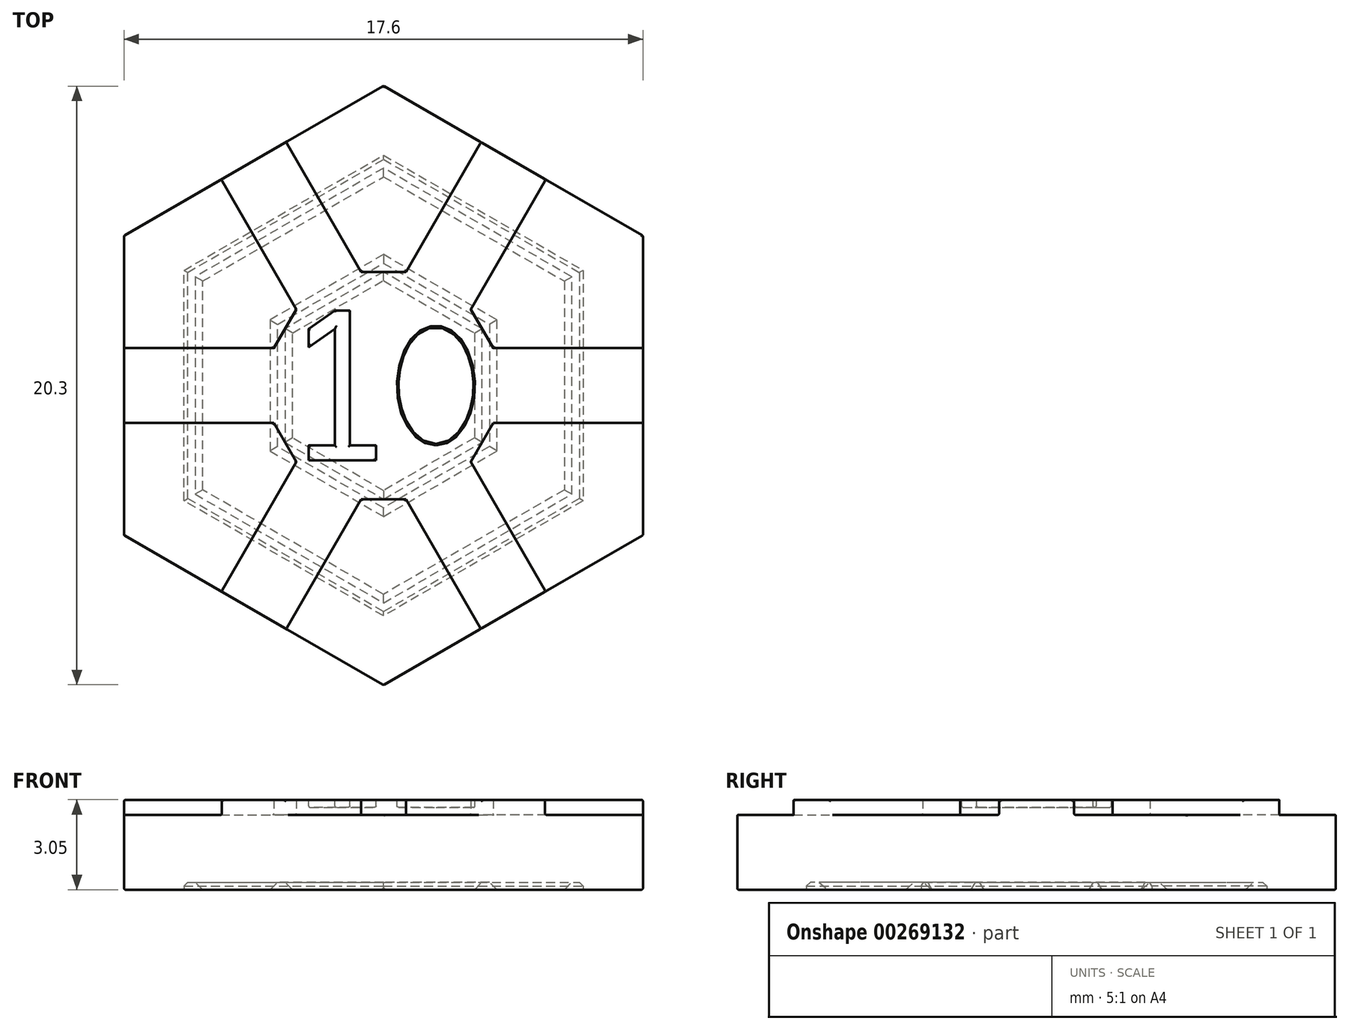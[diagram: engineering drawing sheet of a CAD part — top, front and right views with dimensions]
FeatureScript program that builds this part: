
annotation { "Feature Type Name" : "Feature", "Feature Type Description" : "" }
export const myFeature = defineFeature(function(context is Context, id is Id, definition is map)
    precondition{}
    {
        {
            var Q0;
            Q0=qCreatedBy(makeId("Top.planeOp"),FACE);
            var sketch = newSketch(context, id + "F0", { "sketchPlane" : qUnion([Q0])});
            skLineSegment(sketch, "E0", {"start": v(-8.8, -5.08) * mm, "end": v(-8.8, 5.08) * mm});
            skLineSegment(sketch, "E1", {"start": v(-8.8, 5.08) * mm, "end": v(0, 10.16) * mm});
            skLineSegment(sketch, "E2", {"start": v(0, 10.16) * mm, "end": v(8.8, 5.08) * mm});
            skLineSegment(sketch, "E3", {"start": v(8.8, 5.08) * mm, "end": v(8.8, -5.08) * mm});
            skLineSegment(sketch, "E4", {"start": v(8.8, -5.08) * mm, "end": v(0, -10.16) * mm});
            skLineSegment(sketch, "E5", {"start": v(0, -10.16) * mm, "end": v(-8.8, -5.08) * mm});
            skSolve(sketch);
        }
        {
            var Q0;
            Q0 = qSketchRegion(id + "F0", true);
            extrude(context, id + "F1", {"entities" : qUnion([Q0]), "oppositeDirection" : true, "depth" : 2.54 * mm});
        }
        {
            var Q0;
            Q0=makeQuery(id+"F1.opExtrude","CAP_FACE",FACE,{"disambiguationData":[OSD([sQuery(id+"F0.wireOp",EDGE,"E0"),sQuery(id+"F0.wireOp",EDGE,"E1"),sQuery(id+"F0.wireOp",EDGE,"E2"),sQuery(id+"F0.wireOp",EDGE,"E3"),sQuery(id+"F0.wireOp",EDGE,"E4"),sQuery(id+"F0.wireOp",EDGE,"E5")])],"isStart":true});
            var sketch = newSketch(context, id + "F2", { "sketchPlane" : qUnion([Q0])});
            skLineSegment(sketch, "E6", {"start": v(-3.3, -8.25) * mm, "end": v(-0.76, -3.86) * mm});
            skLineSegment(sketch, "E7", {"start": v(-5.5, -6.98) * mm, "end": v(-2.96, -2.59) * mm});
            skLineSegment(sketch, "E8", {"start": v(-3.3, -8.25) * mm, "end": v(-5.5, -6.98) * mm});
            skLineSegment(sketch, "E9", {"start": v(-8.8, 1.27) * mm, "end": v(-3.72, 1.27) * mm});
            skLineSegment(sketch, "E10", {"start": v(-8.8, -1.27) * mm, "end": v(-3.72, -1.27) * mm});
            skLineSegment(sketch, "E11", {"start": v(-8.8, -1.27) * mm, "end": v(-8.8, 1.27) * mm});
            skLineSegment(sketch, "E12", {"start": v(3.3, 8.26) * mm, "end": v(0.76, 3.86) * mm});
            skLineSegment(sketch, "E13", {"start": v(5.5, 6.99) * mm, "end": v(2.96, 2.59) * mm});
            skLineSegment(sketch, "E14", {"start": v(-5.5, 6.99) * mm, "end": v(-2.96, 2.59) * mm});
            skLineSegment(sketch, "E15", {"start": v(-3.3, 8.26) * mm, "end": v(-0.76, 3.86) * mm});
            skLineSegment(sketch, "E16", {"start": v(8.8, 1.27) * mm, "end": v(3.72, 1.27) * mm});
            skLineSegment(sketch, "E17", {"start": v(8.8, -1.27) * mm, "end": v(3.72, -1.27) * mm});
            skLineSegment(sketch, "E18", {"start": v(5.5, -6.98) * mm, "end": v(2.96, -2.59) * mm});
            skLineSegment(sketch, "E19", {"start": v(3.3, -8.25) * mm, "end": v(0.76, -3.86) * mm});
            skLineSegment(sketch, "E20", {"start": v(-5.5, 6.99) * mm, "end": v(-3.3, 8.26) * mm});
            skLineSegment(sketch, "E21", {"start": v(3.3, 8.25) * mm, "end": v(5.5, 6.98) * mm});
            skLineSegment(sketch, "E22", {"start": v(8.8, 1.27) * mm, "end": v(8.8, -1.27) * mm});
            skLineSegment(sketch, "E23", {"start": v(5.5, -6.98) * mm, "end": v(3.3, -8.25) * mm});
            skLineSegment(sketch, "E24", {"start": v(-0.76, 3.86) * mm, "end": v(0.76, 3.86) * mm});
            skLineSegment(sketch, "E25", {"start": v(2.96, 2.59) * mm, "end": v(3.72, 1.27) * mm});
            skLineSegment(sketch, "E26", {"start": v(3.72, -1.27) * mm, "end": v(2.96, -2.59) * mm});
            skLineSegment(sketch, "E27", {"start": v(0.76, -3.86) * mm, "end": v(-0.76, -3.86) * mm});
            skLineSegment(sketch, "E28", {"start": v(-2.96, -2.59) * mm, "end": v(-3.72, -1.27) * mm});
            skLineSegment(sketch, "E29", {"start": v(-2.96, 2.59) * mm, "end": v(-3.72, 1.27) * mm});
            skSolve(sketch);
        }
        {
            var Q0;
            Q0=makeQuery(id+"F2.imprint","IMPRINT",FACE,{"disambiguationData":[TD([[makeQuery(id+"F2.imprint","IMPRINT",EDGE,{"derivedFrom":sQuery(id+"F2.wireOp",EDGE,"E6")}),1.0]])]});
            extrude(context, id + "F3", {"entities" : qUnion([Q0]), "operationType" : NewBodyOperationType.ADD, "depth" : 0.5 * mm});
        }
        {
            var Q0;
            Q0=makeQuery(id+"F3.opExtrude","CAP_FACE",FACE,{"disambiguationData":[OSD([sQuery(id+"F2.wireOp",EDGE,"E6"),sQuery(id+"F2.wireOp",EDGE,"E7"),sQuery(id+"F2.wireOp",EDGE,"E8"),sQuery(id+"F2.wireOp",EDGE,"E9"),sQuery(id+"F2.wireOp",EDGE,"E10"),sQuery(id+"F2.wireOp",EDGE,"E11"),sQuery(id+"F2.wireOp",EDGE,"E12"),sQuery(id+"F2.wireOp",EDGE,"E13"),sQuery(id+"F2.wireOp",EDGE,"E14"),sQuery(id+"F2.wireOp",EDGE,"E15"),sQuery(id+"F2.wireOp",EDGE,"E16"),sQuery(id+"F2.wireOp",EDGE,"E17"),sQuery(id+"F2.wireOp",EDGE,"E18"),sQuery(id+"F2.wireOp",EDGE,"E19"),sQuery(id+"F2.wireOp",EDGE,"E20"),sQuery(id+"F2.wireOp",EDGE,"E21"),sQuery(id+"F2.wireOp",EDGE,"E22"),sQuery(id+"F2.wireOp",EDGE,"E23"),sQuery(id+"F2.wireOp",EDGE,"E24"),sQuery(id+"F2.wireOp",EDGE,"E25"),sQuery(id+"F2.wireOp",EDGE,"E26"),sQuery(id+"F2.wireOp",EDGE,"E27"),sQuery(id+"F2.wireOp",EDGE,"E28"),sQuery(id+"F2.wireOp",EDGE,"E29")])],"isStart":false});
            var sketch = newSketch(context, id + "F4", { "sketchPlane" : qUnion([Q0])});
            skLineSegment(sketch, "E30", {"start": v(-2.54, -2.54) * mm, "end": v(-0.25, -2.54) * mm});
            skLineSegment(sketch, "E31", {"start": v(-0.25, -2.54) * mm, "end": v(-0.25, -2.03) * mm});
            skLineSegment(sketch, "E32", {"start": v(-0.25, -2.03) * mm, "end": v(-1.14, -2.03) * mm});
            skLineSegment(sketch, "E33", {"start": v(-1.14, -2.03) * mm, "end": v(-1.14, 2.54) * mm});
            skLineSegment(sketch, "E34", {"start": v(-1.14, 2.54) * mm, "end": v(-1.65, 2.54) * mm});
            skLineSegment(sketch, "E35", {"start": v(-2.54, -2.54) * mm, "end": v(-2.54, -2.03) * mm});
            skLineSegment(sketch, "E36", {"start": v(-2.54, -2.03) * mm, "end": v(-1.65, -2.03) * mm});
            skLineSegment(sketch, "E37", {"start": v(-1.65, -2.03) * mm, "end": v(-1.65, 1.92) * mm});
            skLineSegment(sketch, "E38", {"start": v(-1.65, 1.92) * mm, "end": v(-2.54, 1.3) * mm});
            skLineSegment(sketch, "E39", {"start": v(-2.54, 1.3) * mm, "end": v(-2.54, 1.92) * mm});
            skLineSegment(sketch, "E40", {"start": v(-2.54, 1.92) * mm, "end": v(-1.65, 2.54) * mm});
            skSolve(sketch);
        }
        {
            var Q0;
            Q0 = qSketchRegion(id + "F4", true);
            extrude(context, id + "F5", {"entities" : qUnion([Q0]), "operationType" : NewBodyOperationType.REMOVE, "oppositeDirection" : true, "depth" : 0.25 * mm});
        }
        {
            var Q0;
            Q0=makeQuery(id+"F1.opExtrude","CAP_FACE",FACE,{"disambiguationData":[OSD([sQuery(id+"F0.wireOp",EDGE,"E0"),sQuery(id+"F0.wireOp",EDGE,"E1"),sQuery(id+"F0.wireOp",EDGE,"E2"),sQuery(id+"F0.wireOp",EDGE,"E3"),sQuery(id+"F0.wireOp",EDGE,"E4"),sQuery(id+"F0.wireOp",EDGE,"E5")])],"isStart":false});
            var sketch = newSketch(context, id + "F6", { "sketchPlane" : qUnion([Q0])});
            skLineSegment(sketch, "E41.0", {"start": v(6.26, -3.61) * mm, "end": v(6.26, 3.61) * mm});
            skLineSegment(sketch, "E41.1", {"start": v(0, 7.23) * mm, "end": v(-6.26, 3.61) * mm});
            skLineSegment(sketch, "E41.2", {"start": v(-6.26, 3.61) * mm, "end": v(-6.26, -3.61) * mm});
            skLineSegment(sketch, "E41.3", {"start": v(6.26, 3.61) * mm, "end": v(0, 7.23) * mm});
            skLineSegment(sketch, "E41.4", {"start": v(-6.26, -3.61) * mm, "end": v(0, -7.23) * mm});
            skLineSegment(sketch, "E41.5", {"start": v(0, -7.23) * mm, "end": v(6.26, -3.61) * mm});
            skLineSegment(sketch, "E42.0", {"start": v(6.77, -3.9) * mm, "end": v(6.77, 3.9) * mm});
            skLineSegment(sketch, "E42.1", {"start": v(0, 7.81) * mm, "end": v(-6.77, 3.9) * mm});
            skLineSegment(sketch, "E42.2", {"start": v(-6.77, 3.9) * mm, "end": v(-6.77, -3.9) * mm});
            skLineSegment(sketch, "E42.3", {"start": v(6.77, 3.9) * mm, "end": v(0, 7.81) * mm});
            skLineSegment(sketch, "E42.4", {"start": v(-6.77, -3.9) * mm, "end": v(0, -7.81) * mm});
            skLineSegment(sketch, "E42.5", {"start": v(0, -7.81) * mm, "end": v(6.77, -3.9) * mm});
            skSolve(sketch);
        }
        {
            var Q0;
            Q0 = qSketchRegion(id + "F6", true);
            extrude(context, id + "F7", {"entities" : qUnion([Q0]), "operationType" : NewBodyOperationType.REMOVE, "oppositeDirection" : true, "depth" : 0.25 * mm});
        }
        {
            var Q0;
            Q0=makeQuery(id+"F7.boolean.opBoolean","SPLIT",FACE,{"disambiguationData":[TD([makeQuery(id+"F7.opExtrude","SWEPT_FACE",FACE,{"disambiguationData":[OSD([sQuery(id+"F6.wireOp",EDGE,"E41.0")])]})])],"derivedFrom":makeQuery(id+"F1.opExtrude","CAP_FACE",FACE,{"disambiguationData":[OSD([sQuery(id+"F0.wireOp",EDGE,"E0"),sQuery(id+"F0.wireOp",EDGE,"E1"),sQuery(id+"F0.wireOp",EDGE,"E2"),sQuery(id+"F0.wireOp",EDGE,"E3"),sQuery(id+"F0.wireOp",EDGE,"E4"),sQuery(id+"F0.wireOp",EDGE,"E5")])],"isStart":false})});
            var sketch = newSketch(context, id + "F8", { "sketchPlane" : qUnion([Q0])});
            skLineSegment(sketch, "E43.0", {"start": v(-3.72, -2.15) * mm, "end": v(0, -4.3) * mm});
            skLineSegment(sketch, "E43.1", {"start": v(3.72, -2.15) * mm, "end": v(3.72, 2.15) * mm});
            skLineSegment(sketch, "E43.2", {"start": v(3.72, 2.15) * mm, "end": v(0, 4.3) * mm});
            skLineSegment(sketch, "E43.3", {"start": v(0, -4.3) * mm, "end": v(3.72, -2.15) * mm});
            skLineSegment(sketch, "E43.4", {"start": v(0, 4.3) * mm, "end": v(-3.72, 2.15) * mm});
            skLineSegment(sketch, "E43.5", {"start": v(-3.72, 2.15) * mm, "end": v(-3.72, -2.15) * mm});
            skLineSegment(sketch, "E44.0", {"start": v(0, -3.7) * mm, "end": v(3.21, -1.85) * mm});
            skLineSegment(sketch, "E44.1", {"start": v(3.21, 1.85) * mm, "end": v(0, 3.7) * mm});
            skLineSegment(sketch, "E44.2", {"start": v(0, 3.7) * mm, "end": v(-3.21, 1.85) * mm});
            skLineSegment(sketch, "E44.3", {"start": v(3.21, -1.85) * mm, "end": v(3.21, 1.85) * mm});
            skLineSegment(sketch, "E44.4", {"start": v(-3.21, 1.85) * mm, "end": v(-3.21, -1.85) * mm});
            skLineSegment(sketch, "E44.5", {"start": v(-3.21, -1.85) * mm, "end": v(0, -3.7) * mm});
            skSolve(sketch);
        }
        {
            var Q0;
            Q0 = qSketchRegion(id + "F8", true);
            extrude(context, id + "F9", {"entities" : qUnion([Q0]), "operationType" : NewBodyOperationType.REMOVE, "oppositeDirection" : true, "depth" : 0.25 * mm});
        }
        {
            var Q0;
            Q0=makeQuery(id+"F7.boolean.opBoolean","COPY",FACE,{"derivedFrom":makeQuery(id+"F7.opExtrude","CAP_FACE",FACE,{"disambiguationData":[OSD([sQuery(id+"F6.wireOp",EDGE,"E41.0"),sQuery(id+"F6.wireOp",EDGE,"E41.1"),sQuery(id+"F6.wireOp",EDGE,"E41.2"),sQuery(id+"F6.wireOp",EDGE,"E41.3"),sQuery(id+"F6.wireOp",EDGE,"E41.4"),sQuery(id+"F6.wireOp",EDGE,"E41.5"),sQuery(id+"F6.wireOp",EDGE,"E42.0"),sQuery(id+"F6.wireOp",EDGE,"E42.1"),sQuery(id+"F6.wireOp",EDGE,"E42.2"),sQuery(id+"F6.wireOp",EDGE,"E42.3"),sQuery(id+"F6.wireOp",EDGE,"E42.4"),sQuery(id+"F6.wireOp",EDGE,"E42.5")])],"isStart":false})});
            var Q1;
            Q1=makeQuery(id+"F9.boolean.opBoolean","COPY",FACE,{"derivedFrom":makeQuery(id+"F9.opExtrude","CAP_FACE",FACE,{"disambiguationData":[OSD([sQuery(id+"F8.wireOp",EDGE,"E43.0"),sQuery(id+"F8.wireOp",EDGE,"E43.1"),sQuery(id+"F8.wireOp",EDGE,"E43.2"),sQuery(id+"F8.wireOp",EDGE,"E43.3"),sQuery(id+"F8.wireOp",EDGE,"E43.4"),sQuery(id+"F8.wireOp",EDGE,"E43.5"),sQuery(id+"F8.wireOp",EDGE,"E44.0"),sQuery(id+"F8.wireOp",EDGE,"E44.1"),sQuery(id+"F8.wireOp",EDGE,"E44.2"),sQuery(id+"F8.wireOp",EDGE,"E44.3"),sQuery(id+"F8.wireOp",EDGE,"E44.4"),sQuery(id+"F8.wireOp",EDGE,"E44.5")])],"isStart":false})});
            var Q2;
            Q2=makeQuery(id+"F9.boolean.opBoolean","SPLIT",FACE,{"disambiguationData":[TD([makeQuery(id+"F9.opExtrude","SWEPT_FACE",FACE,{"disambiguationData":[OSD([sQuery(id+"F8.wireOp",EDGE,"E44.0")])]})])],"derivedFrom":makeQuery(id+"F7.boolean.opBoolean","SPLIT",FACE,{"disambiguationData":[TD([makeQuery(id+"F7.opExtrude","SWEPT_FACE",FACE,{"disambiguationData":[OSD([sQuery(id+"F6.wireOp",EDGE,"E41.0")])]})])],"derivedFrom":makeQuery(id+"F1.opExtrude","CAP_FACE",FACE,{"disambiguationData":[OSD([sQuery(id+"F0.wireOp",EDGE,"E0"),sQuery(id+"F0.wireOp",EDGE,"E1"),sQuery(id+"F0.wireOp",EDGE,"E2"),sQuery(id+"F0.wireOp",EDGE,"E3"),sQuery(id+"F0.wireOp",EDGE,"E4"),sQuery(id+"F0.wireOp",EDGE,"E5")])],"isStart":false})})});
            var Q3;
            {var subQ1=makeQuery(id+"F7.opExtrude","SWEPT_FACE",FACE,{"disambiguationData":[OSD([sQuery(id+"F6.wireOp",EDGE,"E41.0")])]});Q3=makeQuery(id+"F9.boolean.opBoolean","SPLIT",FACE,{"disambiguationData":[TD([makeQuery(id+"F7.boolean.opBoolean","COPY",FACE,{"derivedFrom":subQ1})])],"derivedFrom":makeQuery(id+"F7.boolean.opBoolean","SPLIT",FACE,{"disambiguationData":[TD([subQ1])],"derivedFrom":makeQuery(id+"F1.opExtrude","CAP_FACE",FACE,{"disambiguationData":[OSD([sQuery(id+"F0.wireOp",EDGE,"E0"),sQuery(id+"F0.wireOp",EDGE,"E1"),sQuery(id+"F0.wireOp",EDGE,"E2"),sQuery(id+"F0.wireOp",EDGE,"E3"),sQuery(id+"F0.wireOp",EDGE,"E4"),sQuery(id+"F0.wireOp",EDGE,"E5")])],"isStart":false})})});}
            var Q4;
            Q4=makeQuery(id+"F7.boolean.opBoolean","COPY",EDGE,{"derivedFrom":makeQuery(id+"F7.opExtrude","CAP_EDGE",EDGE,{"disambiguationData":[OSD([sQuery(id+"F6.wireOp",EDGE,"E42.5")])],"isStart":true})});
            var Q5;
            Q5=makeQuery(id+"F7.boolean.opBoolean","COPY",EDGE,{"derivedFrom":makeQuery(id+"F7.opExtrude","CAP_EDGE",EDGE,{"disambiguationData":[OSD([sQuery(id+"F6.wireOp",EDGE,"E42.4")])],"isStart":true})});
            var Q6;
            Q6=makeQuery(id+"F7.boolean.opBoolean","COPY",EDGE,{"derivedFrom":makeQuery(id+"F7.opExtrude","CAP_EDGE",EDGE,{"disambiguationData":[OSD([sQuery(id+"F6.wireOp",EDGE,"E42.2")])],"isStart":true})});
            var Q7;
            Q7=makeQuery(id+"F7.boolean.opBoolean","COPY",EDGE,{"derivedFrom":makeQuery(id+"F7.opExtrude","CAP_EDGE",EDGE,{"disambiguationData":[OSD([sQuery(id+"F6.wireOp",EDGE,"E42.1")])],"isStart":true})});
            var Q8;
            Q8=makeQuery(id+"F7.boolean.opBoolean","COPY",EDGE,{"derivedFrom":makeQuery(id+"F7.opExtrude","CAP_EDGE",EDGE,{"disambiguationData":[OSD([sQuery(id+"F6.wireOp",EDGE,"E42.0")])],"isStart":true})});
            var Q9;
            Q9=makeQuery(id+"F7.boolean.opBoolean","COPY",EDGE,{"derivedFrom":makeQuery(id+"F7.opExtrude","CAP_EDGE",EDGE,{"disambiguationData":[OSD([sQuery(id+"F6.wireOp",EDGE,"E42.3")])],"isStart":true})});
            chamfer(context, id + "F10", {"entities" : qUnion([Q0, Q1, Q2, Q3, Q4, Q5, Q6, Q7, Q8, Q9]), "width" : 0.13 * mm, "tangentPropagation" : true});
        }
        {
            var Q0;
            Q0=makeQuery(id+"F3.opExtrude","CAP_FACE",FACE,{"disambiguationData":[OSD([sQuery(id+"F2.wireOp",EDGE,"E6"),sQuery(id+"F2.wireOp",EDGE,"E7"),sQuery(id+"F2.wireOp",EDGE,"E8"),sQuery(id+"F2.wireOp",EDGE,"E9"),sQuery(id+"F2.wireOp",EDGE,"E10"),sQuery(id+"F2.wireOp",EDGE,"E11"),sQuery(id+"F2.wireOp",EDGE,"E12"),sQuery(id+"F2.wireOp",EDGE,"E13"),sQuery(id+"F2.wireOp",EDGE,"E14"),sQuery(id+"F2.wireOp",EDGE,"E15"),sQuery(id+"F2.wireOp",EDGE,"E16"),sQuery(id+"F2.wireOp",EDGE,"E17"),sQuery(id+"F2.wireOp",EDGE,"E18"),sQuery(id+"F2.wireOp",EDGE,"E19"),sQuery(id+"F2.wireOp",EDGE,"E20"),sQuery(id+"F2.wireOp",EDGE,"E21"),sQuery(id+"F2.wireOp",EDGE,"E22"),sQuery(id+"F2.wireOp",EDGE,"E23"),sQuery(id+"F2.wireOp",EDGE,"E24"),sQuery(id+"F2.wireOp",EDGE,"E25"),sQuery(id+"F2.wireOp",EDGE,"E26"),sQuery(id+"F2.wireOp",EDGE,"E27"),sQuery(id+"F2.wireOp",EDGE,"E28"),sQuery(id+"F2.wireOp",EDGE,"E29")])],"isStart":false});
            var sketch = newSketch(context, id + "F11", { "sketchPlane" : qUnion([Q0])});
            skEllipse(sketch, "E45", {"center": v(1.78, 0) * mm, "majorRadius": 2.03 * mm, "minorRadius": 1.32 * mm, "majorAxis": v(0, -1)});
            skFitSpline(sketch, "E46.0", {"points": [v(1.37, -2.5) * mm, v(1.78, -2.56) * mm, v(2.2, -2.5) * mm, v(2.7, -2.26) * mm, v(3.18, -1.75) * mm, v(3.53, -0.93) * mm, v(3.65, 0) * mm, v(3.53, 0.93) * mm, v(3.18, 1.75) * mm, v(2.7, 2.26) * mm, v(2.2, 2.5) * mm, v(1.78, 2.56) * mm, v(1.37, 2.5) * mm, v(0.86, 2.26) * mm, v(0.38, 1.75) * mm, v(0.03, 0.93) * mm, v(-0.1, 0) * mm, v(0.03, -0.93) * mm, v(0.38, -1.75) * mm, v(0.86, -2.26) * mm, v(1.37, -2.5) * mm, v(1.78, -2.56) * mm, v(2.2, -2.5) * mm, v(1.37, -2.5) * mm]});
            skLineSegment(sketch, "E47", {"start": v(-1.14, 2.54) * mm, "end": v(3.56, 2.54) * mm, "construction": true});
            skLineSegment(sketch, "E48", {"start": v(-0.25, -2.54) * mm, "end": v(3.72, -2.54) * mm, "construction": true});
            skSolve(sketch);
        }
        {
            var Q0;
            Q0 = qSketchRegion(id + "F11", true);
            extrude(context, id + "F12", {"entities" : qUnion([Q0]), "operationType" : NewBodyOperationType.REMOVE, "oppositeDirection" : true, "depth" : 0.25 * mm});
        }
        {
            var Q0;
            {var subQ0=sQuery(id+"F0.wireOp",EDGE,"E3");var subQ1=sQuery(id+"F0.wireOp",EDGE,"E2");Q0=makeQuery(id+"F3.boolean.opBoolean","SPLIT",FACE,{"disambiguationData":[TD([makeQuery(id+"F3.opExtrude","SWEPT_FACE",FACE,{"disambiguationData":[OSD([sQuery(id+"F2.wireOp",EDGE,"E13")])]})])],"derivedFrom":makeQuery(id+"F1.opExtrude","CAP_FACE",FACE,{"disambiguationData":[OSD([sQuery(id+"F0.wireOp",EDGE,"E0"),sQuery(id+"F0.wireOp",EDGE,"E1"),subQ1,subQ0,sQuery(id+"F0.wireOp",EDGE,"E4"),sQuery(id+"F0.wireOp",EDGE,"E5")])],"isStart":true})});}
            var Q1;
            {var subQ0=sQuery(id+"F0.wireOp",EDGE,"E2");var subQ1=sQuery(id+"F0.wireOp",EDGE,"E1");Q1=makeQuery(id+"F3.boolean.opBoolean","SPLIT",FACE,{"disambiguationData":[TD([makeQuery(id+"F3.opExtrude","SWEPT_FACE",FACE,{"disambiguationData":[OSD([sQuery(id+"F2.wireOp",EDGE,"E12")])]})])],"derivedFrom":makeQuery(id+"F1.opExtrude","CAP_FACE",FACE,{"disambiguationData":[OSD([sQuery(id+"F0.wireOp",EDGE,"E0"),subQ1,subQ0,sQuery(id+"F0.wireOp",EDGE,"E3"),sQuery(id+"F0.wireOp",EDGE,"E4"),sQuery(id+"F0.wireOp",EDGE,"E5")])],"isStart":true})});}
            var Q2;
            {var subQ0=sQuery(id+"F0.wireOp",EDGE,"E1");var subQ1=sQuery(id+"F0.wireOp",EDGE,"E0");Q2=makeQuery(id+"F3.boolean.opBoolean","SPLIT",FACE,{"disambiguationData":[TD([makeQuery(id+"F3.opExtrude","SWEPT_FACE",FACE,{"disambiguationData":[OSD([sQuery(id+"F2.wireOp",EDGE,"E9")])]})])],"derivedFrom":makeQuery(id+"F1.opExtrude","CAP_FACE",FACE,{"disambiguationData":[OSD([subQ1,subQ0,sQuery(id+"F0.wireOp",EDGE,"E2"),sQuery(id+"F0.wireOp",EDGE,"E3"),sQuery(id+"F0.wireOp",EDGE,"E4"),sQuery(id+"F0.wireOp",EDGE,"E5")])],"isStart":true})});}
            var Q3;
            {var subQ0=sQuery(id+"F0.wireOp",EDGE,"E5");var subQ1=sQuery(id+"F0.wireOp",EDGE,"E0");Q3=makeQuery(id+"F3.boolean.opBoolean","SPLIT",FACE,{"disambiguationData":[TD([makeQuery(id+"F3.opExtrude","SWEPT_FACE",FACE,{"disambiguationData":[OSD([sQuery(id+"F2.wireOp",EDGE,"E7")])]})])],"derivedFrom":makeQuery(id+"F1.opExtrude","CAP_FACE",FACE,{"disambiguationData":[OSD([subQ1,sQuery(id+"F0.wireOp",EDGE,"E1"),sQuery(id+"F0.wireOp",EDGE,"E2"),sQuery(id+"F0.wireOp",EDGE,"E3"),sQuery(id+"F0.wireOp",EDGE,"E4"),subQ0])],"isStart":true})});}
            var Q4;
            {var subQ0=sQuery(id+"F0.wireOp",EDGE,"E5");var subQ1=sQuery(id+"F0.wireOp",EDGE,"E4");Q4=makeQuery(id+"F3.boolean.opBoolean","SPLIT",FACE,{"disambiguationData":[TD([makeQuery(id+"F3.opExtrude","SWEPT_FACE",FACE,{"disambiguationData":[OSD([sQuery(id+"F2.wireOp",EDGE,"E6")])]})])],"derivedFrom":makeQuery(id+"F1.opExtrude","CAP_FACE",FACE,{"disambiguationData":[OSD([sQuery(id+"F0.wireOp",EDGE,"E0"),sQuery(id+"F0.wireOp",EDGE,"E1"),sQuery(id+"F0.wireOp",EDGE,"E2"),sQuery(id+"F0.wireOp",EDGE,"E3"),subQ1,subQ0])],"isStart":true})});}
            var Q5;
            {var subQ0=sQuery(id+"F0.wireOp",EDGE,"E4");var subQ1=sQuery(id+"F0.wireOp",EDGE,"E3");Q5=makeQuery(id+"F3.boolean.opBoolean","SPLIT",FACE,{"disambiguationData":[TD([makeQuery(id+"F3.opExtrude","SWEPT_FACE",FACE,{"disambiguationData":[OSD([sQuery(id+"F2.wireOp",EDGE,"E17")])]})])],"derivedFrom":makeQuery(id+"F1.opExtrude","CAP_FACE",FACE,{"disambiguationData":[OSD([sQuery(id+"F0.wireOp",EDGE,"E0"),sQuery(id+"F0.wireOp",EDGE,"E1"),sQuery(id+"F0.wireOp",EDGE,"E2"),subQ1,subQ0,sQuery(id+"F0.wireOp",EDGE,"E5")])],"isStart":true})});}
            fillet(context, id + "F13", {"entities" : qUnion([Q0, Q1, Q2, Q3, Q4, Q5]), "radius" : 0.05 * mm, "tangentPropagation" : true, "allowEdgeOverflow" : false});
        }
        {
            var Q0;
            Q0=makeQuery(id+"F5.boolean.opBoolean","COPY",FACE,{"derivedFrom":makeQuery(id+"F5.opExtrude","CAP_FACE",FACE,{"disambiguationData":[OSD([sQuery(id+"F4.wireOp",EDGE,"E30"),sQuery(id+"F4.wireOp",EDGE,"E31"),sQuery(id+"F4.wireOp",EDGE,"E32"),sQuery(id+"F4.wireOp",EDGE,"E33"),sQuery(id+"F4.wireOp",EDGE,"E34"),sQuery(id+"F4.wireOp",EDGE,"E35"),sQuery(id+"F4.wireOp",EDGE,"E36"),sQuery(id+"F4.wireOp",EDGE,"E37"),sQuery(id+"F4.wireOp",EDGE,"E38"),sQuery(id+"F4.wireOp",EDGE,"E39"),sQuery(id+"F4.wireOp",EDGE,"E40")])],"isStart":false})});
            fillet(context, id + "F14", {"entities" : qUnion([Q0]), "radius" : 0.05 * mm, "tangentPropagation" : true, "allowEdgeOverflow" : false});
        }
        {
            var Q0;
            Q0=makeQuery(id+"F12.boolean.opBoolean","COPY",FACE,{"derivedFrom":makeQuery(id+"F12.opExtrude","CAP_FACE",FACE,{"disambiguationData":[OSD([sQuery(id+"F11.wireOp",EDGE,"E45"),sQuery(id+"F11.wireOp",EDGE,"E46.0")])],"isStart":false})});
            fillet(context, id + "F15", {"entities" : qUnion([Q0]), "radius" : 0.05 * mm, "tangentPropagation" : true, "allowEdgeOverflow" : false});
        }
        {
            var Q0;
            Q0=makeQuery(id+"F3.boolean.opBoolean","MERGE",FACE,{"derivedFrom":[makeQuery(id+"F1.opExtrude","SWEPT_FACE",FACE,{"disambiguationData":[OSD([sQuery(id+"F0.wireOp",EDGE,"E1")])]}),makeQuery(id+"F3.opExtrude","SWEPT_FACE",FACE,{"disambiguationData":[OSD([sQuery(id+"F2.wireOp",EDGE,"E20")])]})]});
            var Q1;
            Q1=makeQuery(id+"F3.boolean.opBoolean","MERGE",FACE,{"derivedFrom":[makeQuery(id+"F1.opExtrude","SWEPT_FACE",FACE,{"disambiguationData":[OSD([sQuery(id+"F0.wireOp",EDGE,"E0")])]}),makeQuery(id+"F3.opExtrude","SWEPT_FACE",FACE,{"disambiguationData":[OSD([sQuery(id+"F2.wireOp",EDGE,"E11")])]})]});
            var Q2;
            Q2=makeQuery(id+"F3.boolean.opBoolean","MERGE",FACE,{"derivedFrom":[makeQuery(id+"F1.opExtrude","SWEPT_FACE",FACE,{"disambiguationData":[OSD([sQuery(id+"F0.wireOp",EDGE,"E5")])]}),makeQuery(id+"F3.opExtrude","SWEPT_FACE",FACE,{"disambiguationData":[OSD([sQuery(id+"F2.wireOp",EDGE,"E8")])]})]});
            var Q3;
            Q3=makeQuery(id+"F3.boolean.opBoolean","MERGE",FACE,{"derivedFrom":[makeQuery(id+"F1.opExtrude","SWEPT_FACE",FACE,{"disambiguationData":[OSD([sQuery(id+"F0.wireOp",EDGE,"E2")])]}),makeQuery(id+"F3.opExtrude","SWEPT_FACE",FACE,{"disambiguationData":[OSD([sQuery(id+"F2.wireOp",EDGE,"E21")])]})]});
            var Q4;
            Q4=makeQuery(id+"F3.boolean.opBoolean","MERGE",FACE,{"derivedFrom":[makeQuery(id+"F1.opExtrude","SWEPT_FACE",FACE,{"disambiguationData":[OSD([sQuery(id+"F0.wireOp",EDGE,"E3")])]}),makeQuery(id+"F3.opExtrude","SWEPT_FACE",FACE,{"disambiguationData":[OSD([sQuery(id+"F2.wireOp",EDGE,"E22")])]})]});
            var Q5;
            Q5=makeQuery(id+"F3.boolean.opBoolean","MERGE",FACE,{"derivedFrom":[makeQuery(id+"F1.opExtrude","SWEPT_FACE",FACE,{"disambiguationData":[OSD([sQuery(id+"F0.wireOp",EDGE,"E4")])]}),makeQuery(id+"F3.opExtrude","SWEPT_FACE",FACE,{"disambiguationData":[OSD([sQuery(id+"F2.wireOp",EDGE,"E23")])]})]});
            fillet(context, id + "F16", {"entities" : qUnion([Q0, Q1, Q2, Q3, Q4, Q5]), "radius" : 0.05 * mm, "tangentPropagation" : true, "allowEdgeOverflow" : false});
        }
    });
